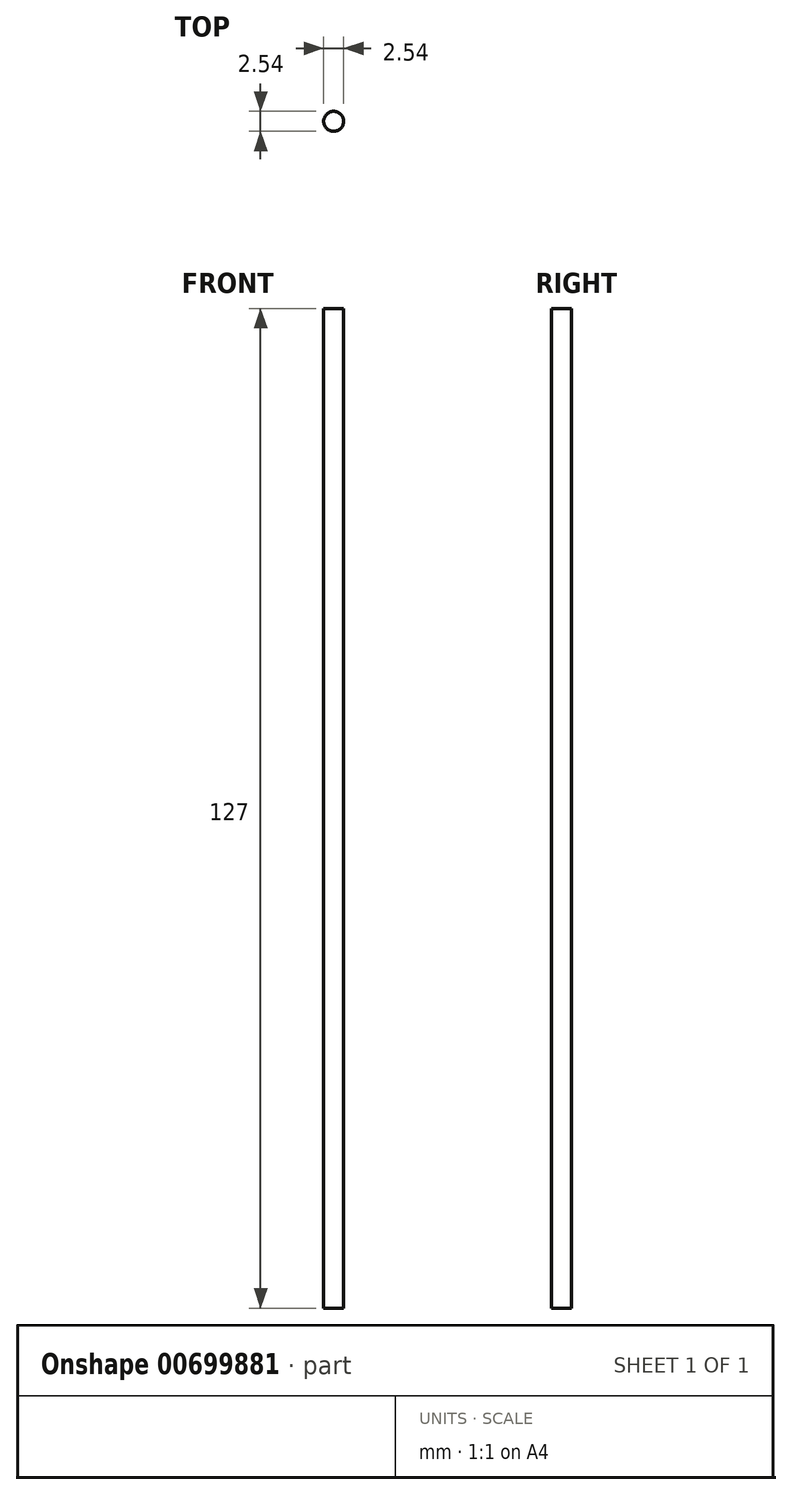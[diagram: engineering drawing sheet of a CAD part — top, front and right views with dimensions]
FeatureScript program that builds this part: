
annotation { "Feature Type Name" : "Feature", "Feature Type Description" : "" }
export const myFeature = defineFeature(function(context is Context, id is Id, definition is map)
    precondition{}
    {
        {
            var Q0;
            Q0=qCreatedBy(makeId("Top.planeOp"),FACE);
            var sketch = newSketch(context, id + "F0", { "sketchPlane" : qUnion([Q0])});
            skCircle(sketch, "E0", {"center": v(0, 0) * mm, "radius": 1.27 * mm});
            skSolve(sketch);
        }
        {
            var Q0;
            Q0=makeQuery(id+"F0.imprint","IMPRINT",FACE,{"disambiguationData":[TD([[makeQuery(id+"F0.imprint","IMPRINT",EDGE,{"derivedFrom":sQuery(id+"F0.wireOp",EDGE,"E0")}),1.0]])]});
            extrude(context, id + "F1", {"entities" : qUnion([Q0]), "depth" : 127 * mm, "offsetDistance" : 25.4 * mm});
        }
    });
